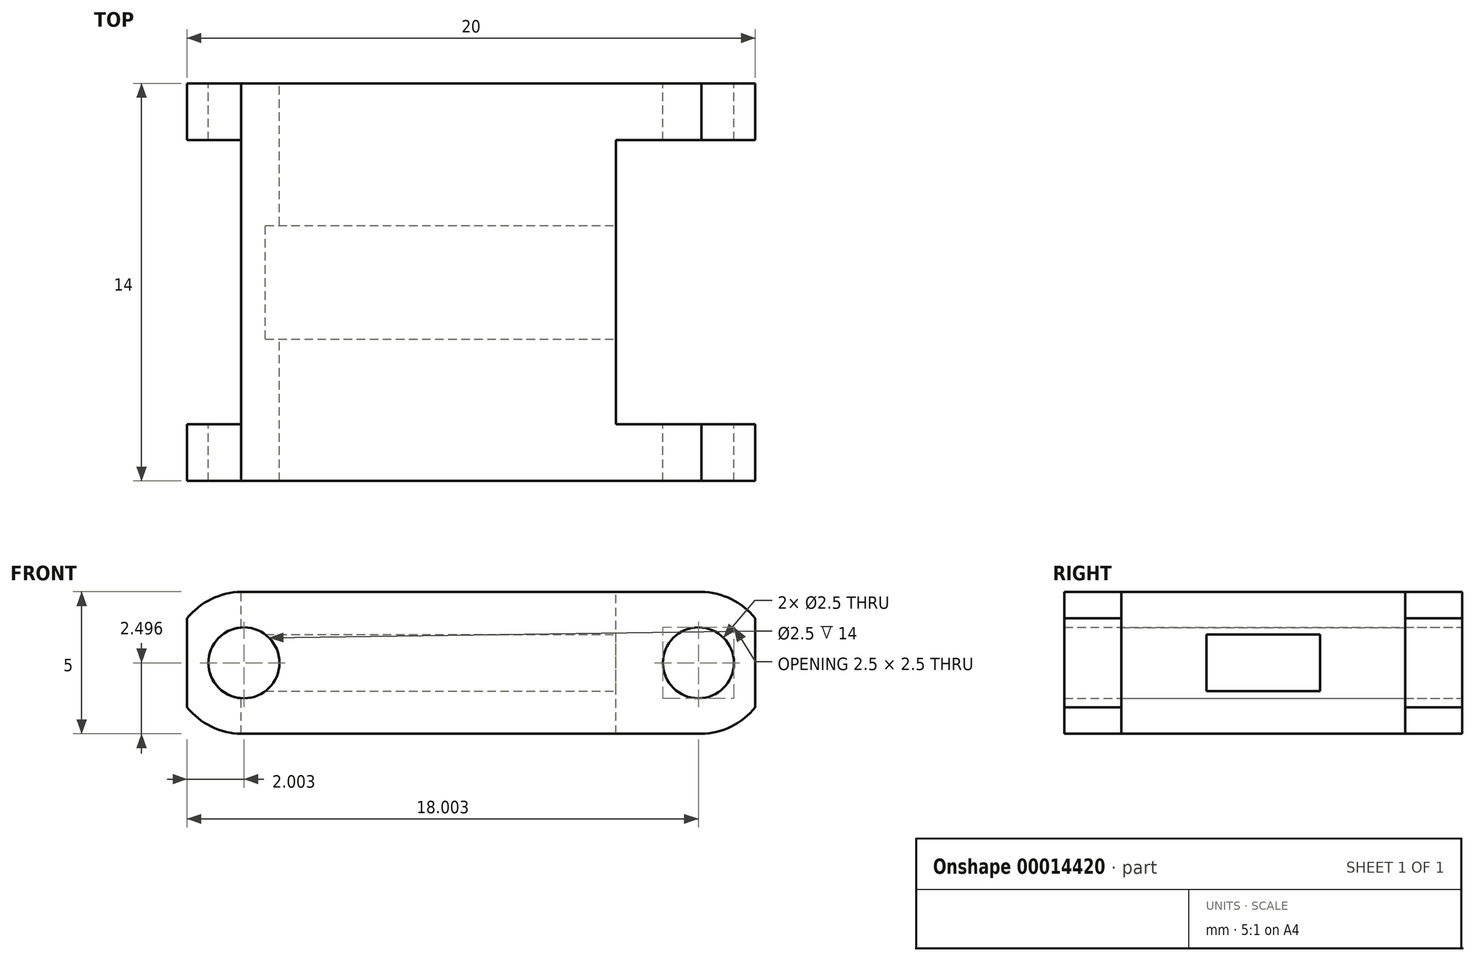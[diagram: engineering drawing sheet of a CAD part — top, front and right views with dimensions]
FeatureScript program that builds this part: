
annotation { "Feature Type Name" : "Feature", "Feature Type Description" : "" }
export const myFeature = defineFeature(function(context is Context, id is Id, definition is map)
    precondition{}
    {
        {
            var Q0;
            Q0=qCreatedBy(makeId("Front.planeOp"),FACE);
            var sketch = newSketch(context, id + "F0", { "sketchPlane" : qUnion([Q0])});
            skLineSegment(sketch, "E0.bottom", {"start": v(33.18, 20.58) * mm, "end": v(53.18, 20.58) * mm});
            skLineSegment(sketch, "E0.top", {"start": v(33.18, 15.58) * mm, "end": v(53.18, 15.58) * mm});
            skLineSegment(sketch, "E0.left", {"start": v(33.18, 20.58) * mm, "end": v(33.18, 15.58) * mm});
            skLineSegment(sketch, "E0.right", {"start": v(53.18, 20.58) * mm, "end": v(53.18, 15.58) * mm});
            skLineSegment(sketch, "E1", {"start": v(43.18, 15.58) * mm, "end": v(43.18, 20.58) * mm, "construction": true});
            skPoint(sketch, "E2", {"position": v(37.18, 20.58) * mm});
            skPoint(sketch, "E3", {"position": v(33.18, 20.58) * mm});
            skLineSegment(sketch, "E4", {"start": v(33.18, 15.58) * mm, "end": v(37.18, 20.58) * mm, "construction": true});
            skLineSegment(sketch, "E5", {"start": v(37.18, 20.58) * mm, "end": v(37.18, 15.58) * mm, "construction": true});
            skLineSegment(sketch, "E6", {"start": v(37.18, 15.58) * mm, "end": v(33.18, 20.58) * mm, "construction": true});
            skCircle(sketch, "E7", {"center": v(35.18, 18.08) * mm, "radius": 1.25 * mm});
            skLineSegment(sketch, "E8", {"start": v(35.18, 18.08) * mm, "end": v(35.18, 20.58) * mm, "construction": true});
            skLineSegment(sketch, "E9", {"start": v(35.18, 20.58) * mm, "end": v(35.18, 15.58) * mm, "construction": true});
            skLineSegment(sketch, "E10", {"start": v(33.18, 18.08) * mm, "end": v(37.18, 18.08) * mm, "construction": true});
            skCircle(sketch, "E11.0.MirrorC", {"center": v(51.18, 18.08) * mm, "radius": 1.25 * mm});
            skArc(sketch, "E12", {"start": v(35.18, 20.58) * mm, "mid": v(32.63, 18.08) * mm, "end": v(35.18, 15.58) * mm});
            skLineSegment(sketch, "E13.0.MirrorCS", {"start": v(53.18, 18.08) * mm, "end": v(49.18, 18.08) * mm, "construction": true});
            skArc(sketch, "E14.0.MirrorCS", {"start": v(51.18, 20.58) * mm, "mid": v(53.73, 18.08) * mm, "end": v(51.18, 15.58) * mm});
            skSolve(sketch);
        }
        {
            var Q0;
            Q0=makeQuery(id+"F0.imprint","IMPRINT",FACE,{"disambiguationData":[TD([[makeQuery(id+"F0.imprint","IMPRINT",EDGE,{"derivedFrom":sQuery(id+"F0.wireOp",EDGE,"E7")}),-1.0]])]});
            extrude(context, id + "F1", {"entities" : qUnion([Q0]), "depth" : 14 * mm});
        }
        {
            var Q0;
            Q0=makeQuery(id+"F1.opExtrude","SWEPT_FACE",FACE,{"disambiguationData":[OSD([sQuery(id+"F0.wireOp",EDGE,"E0.bottom")])]});
            var sketch = newSketch(context, id + "F2", { "sketchPlane" : qUnion([Q0])});
            skLineSegment(sketch, "E15", {"start": v(35.08, -14) * mm, "end": v(35.08, 0) * mm, "construction": true});
            skLineSegment(sketch, "E16", {"start": v(35.08, 0) * mm, "end": v(35.08, -14) * mm, "construction": true});
            skLineSegment(sketch, "E17", {"start": v(43.18, -14) * mm, "end": v(43.18, 0) * mm, "construction": true});
            skPoint(sketch, "E18", {"position": v(35.08, -7) * mm});
            skPoint(sketch, "E19", {"position": v(38.08, -7) * mm});
            skPoint(sketch, "E20.0.MirrorP", {"position": v(48.28, -7) * mm});
            skLineSegment(sketch, "E21", {"start": v(48.28, 0) * mm, "end": v(48.28, -14) * mm});
            skLineSegment(sketch, "E22", {"start": v(38.08, 0) * mm, "end": v(38.08, -14) * mm});
            skLineSegment(sketch, "E23", {"start": v(48.28, -14) * mm, "end": v(38.08, -14) * mm});
            skLineSegment(sketch, "E24", {"start": v(48.28, 0) * mm, "end": v(38.08, 0) * mm});
            skPoint(sketch, "E25", {"position": v(43.18, -12) * mm});
            skPoint(sketch, "E26.0.MirrorP", {"position": v(43.18, -2) * mm});
            skLineSegment(sketch, "E27", {"start": v(43.18, -12) * mm, "end": v(52.18, -12) * mm, "construction": true});
            skLineSegment(sketch, "E28", {"start": v(52.18, -12) * mm, "end": v(34.18, -12) * mm, "construction": true});
            skLineSegment(sketch, "E29", {"start": v(43.18, -2) * mm, "end": v(34.18, -2) * mm, "construction": true});
            skLineSegment(sketch, "E30", {"start": v(34.18, -2) * mm, "end": v(52.18, -2) * mm, "construction": true});
            skLineSegment(sketch, "E31", {"start": v(52.18, -2) * mm, "end": v(38.08, -2) * mm});
            skLineSegment(sketch, "E32.0.MirrorCS", {"start": v(52.18, -12) * mm, "end": v(38.08, -12) * mm});
            skLineSegment(sketch, "E33.0.MirrorCS", {"start": v(34.18, -2) * mm, "end": v(48.28, -2) * mm});
            skLineSegment(sketch, "E34.0.MirrorCS", {"start": v(34.18, -12) * mm, "end": v(48.28, -12) * mm});
            skLineSegment(sketch, "E35", {"start": v(38.08, -2) * mm, "end": v(31.92, -2) * mm});
            skLineSegment(sketch, "E36", {"start": v(38.08, -12) * mm, "end": v(31.58, -12) * mm});
            skLineSegment(sketch, "E37", {"start": v(31.58, -12) * mm, "end": v(31.92, -2) * mm});
            skLineSegment(sketch, "E38", {"start": v(52.18, -12) * mm, "end": v(56.91, -12) * mm});
            skLineSegment(sketch, "E39", {"start": v(52.18, -2) * mm, "end": v(56.94, -2) * mm});
            skLineSegment(sketch, "E40", {"start": v(56.94, -2) * mm, "end": v(56.91, -12) * mm});
            skPoint(sketch, "E41", {"position": v(38.08, -1) * mm});
            skLineSegment(sketch, "E42", {"start": v(43.18, -7) * mm, "end": v(34.34, -7) * mm, "construction": true});
            skPoint(sketch, "E43.start.orphan", {"position": v(32.62, -1) * mm});
            skPoint(sketch, "E44.orphan", {"position": v(32.62, -13) * mm});
            skPoint(sketch, "E45.MirrorCS.end.orphan", {"position": v(31.92, -12) * mm});
            skPoint(sketch, "E46.MirrorCS.start.orphan", {"position": v(38.08, -13) * mm});
            skPoint(sketch, "E47.MirrorCS.end.orphan", {"position": v(53.74, -1) * mm});
            skPoint(sketch, "E47.MirrorCS.start.orphan", {"position": v(48.28, -1) * mm});
            skPoint(sketch, "E48.MirrorCS.end.orphan", {"position": v(54.44, -2) * mm});
            skPoint(sketch, "E49.MirrorCS.end.orphan", {"position": v(53.74, -13) * mm});
            skPoint(sketch, "E49.MirrorCS.start.orphan", {"position": v(48.28, -13) * mm});
            skPoint(sketch, "E50.MirrorCS.end.orphan", {"position": v(54.44, -12) * mm});
            skSolve(sketch);
        }
        {
            var Q0;
            {var subQ5=sQuery(id+"F2.wireOp",EDGE,"E37");Q0=makeQuery(id+"F2.imprint","IMPRINT",FACE,{"disambiguationData":[TD([[makeQuery(id+"F2.imprint","IMPRINT",EDGE,{"derivedFrom":subQ5}),-1.0]])]});}
            var Q1;
            {var subQ3=sQuery(id+"F2.wireOp",EDGE,"E35");var subQ5=sQuery(id+"F2.wireOp",EDGE,"E22");var subQ7=makeQuery(id+"F2.imprint","INTERSECT",VERTEX,{"derivedFrom":[subQ5,sQuery(id+"F2.wireOp",EDGE,"E33.0.MirrorCS"),subQ3]});Q1=makeQuery(id+"F2.imprint","IMPRINT",FACE,{"disambiguationData":[TD([[makeQuery(id+"F2.imprint","IMPRINT",EDGE,{"disambiguationData":[TD([[subQ7,-1.0]])],"derivedFrom":subQ5}),-1.0]])]});}
            var Q2;
            {var subQ3=sQuery(id+"F2.wireOp",EDGE,"E31");var subQ5=sQuery(id+"F2.wireOp",EDGE,"E21");var subQ7=makeQuery(id+"F2.imprint","INTERSECT",VERTEX,{"derivedFrom":[subQ5,subQ3,sQuery(id+"F2.wireOp",EDGE,"E33.0.MirrorCS")]});Q2=makeQuery(id+"F2.imprint","IMPRINT",FACE,{"disambiguationData":[TD([[makeQuery(id+"F2.imprint","IMPRINT",EDGE,{"disambiguationData":[TD([[subQ7,-1.0]])],"derivedFrom":subQ5}),1.0]])]});}
            var Q3;
            {var subQ1=sQuery(id+"F2.wireOp",EDGE,"E38");Q3=makeQuery(id+"F2.imprint","IMPRINT",FACE,{"disambiguationData":[TD([[makeQuery(id+"F2.imprint","IMPRINT",EDGE,{"derivedFrom":subQ1}),1.0]])]});}
            extrude(context, id + "F4", {"entities" : qUnion([Q0, Q1, Q2, Q3]), "operationType" : NewBodyOperationType.REMOVE, "endBound" : BoundingType.THROUGH_ALL, "oppositeDirection" : true, "depth" : 25 * mm});
        }
        {
            var Q0;
            Q0=makeQuery(id+"F4.boolean.opBoolean","COPY",FACE,{"derivedFrom":makeQuery(id+"F4.opExtrude","SWEPT_FACE",FACE,{"disambiguationData":[OSD([sQuery(id+"F2.wireOp",EDGE,"E21")])]})});
            var sketch = newSketch(context, id + "F5", { "sketchPlane" : qUnion([Q0])});
            skPoint(sketch, "E51", {"position": v(-2, 18.08) * mm});
            skPoint(sketch, "E52", {"position": v(-7, 20.58) * mm});
            skLineSegment(sketch, "E53", {"start": v(-2, 18.08) * mm, "end": v(-2, 18.08) * mm});
            skLineSegment(sketch, "E54", {"start": v(-7, 20.58) * mm, "end": v(-7, 15.58) * mm, "construction": true});
            skPoint(sketch, "E55", {"position": v(-7, 18.08) * mm});
            skPoint(sketch, "E56", {"position": v(-5, 18.08) * mm});
            skPoint(sketch, "E57", {"position": v(-7, 19.08) * mm});
            skLineSegment(sketch, "E58", {"start": v(-7, 19.08) * mm, "end": v(-4.52, 19.08) * mm, "construction": true});
            skLineSegment(sketch, "E59", {"start": v(-5, 18.08) * mm, "end": v(-5, 19.08) * mm, "construction": true});
            skLineSegment(sketch, "E60", {"start": v(-7, 19.08) * mm, "end": v(-5, 19.08) * mm});
            skLineSegment(sketch, "E61", {"start": v(-5, 18.08) * mm, "end": v(-5, 19.08) * mm});
            skLineSegment(sketch, "E62.MirrorCS", {"start": v(-7, 19.08) * mm, "end": v(-9, 19.08) * mm});
            skLineSegment(sketch, "E63.MirrorCS", {"start": v(-9, 18.08) * mm, "end": v(-9, 19.08) * mm});
            skLineSegment(sketch, "E64.MirrorCS", {"start": v(-7, 17.08) * mm, "end": v(-5, 17.08) * mm});
            skLineSegment(sketch, "E65.MirrorCS", {"start": v(-7, 17.08) * mm, "end": v(-9, 17.08) * mm});
            skLineSegment(sketch, "E66.MirrorCS", {"start": v(-9, 18.08) * mm, "end": v(-9, 17.08) * mm});
            skLineSegment(sketch, "E67.MirrorCS", {"start": v(-5, 18.08) * mm, "end": v(-5, 17.08) * mm});
            skSolve(sketch);
        }
        {
            var Q0;
            Q0=makeQuery(id+"F5.imprint","IMPRINT",FACE,{"disambiguationData":[TD([[makeQuery(id+"F5.imprint","IMPRINT",EDGE,{"derivedFrom":sQuery(id+"F5.wireOp",EDGE,"E60")}),-1.0]])]});
            extrude(context, id + "F6", {"entities" : qUnion([Q0]), "operationType" : NewBodyOperationType.REMOVE, "endBound" : BoundingType.THROUGH_ALL, "oppositeDirection" : true, "depth" : 25 * mm});
        }
    });
